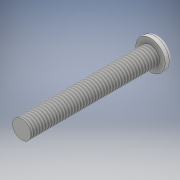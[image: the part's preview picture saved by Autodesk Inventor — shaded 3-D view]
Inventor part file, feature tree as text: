
AUTODESK INVENTOR PART (.ipt)
format: ipt  version: 2018 (Build 220112000, 112)  size: 139,776 bytes
history: native  units: mm
features: sketch x2, revolve x1, fillet x1, extrude x1, thread x1
ambient origin geometry x8: Origin, YZ Plane, XZ Plane, XY Plane, X Axis, Y Axis, Z Axis, Center Point
bodies: Solid1 (feature_tree)
feature tree (6):
  revolve  "Revolution1"  [1 undecoded]
  fillet  "Fillet1"  Radius=2.1mm
  extrude  "Extrusion1"  TaperAngle=90.0deg  [1 undecoded]
  thread  "Thread1"  [1 undecoded]
  sketch  "Sketch1"  dims[d0=2.5mm d1=35.0mm d2=2.1mm]
  sketch  "Sketch2"  dims[d3=4.0mm d4=90.0deg d5=1.0mm d6=0.75mm d7=0.75mm d8=2.7mm d9=2.7mm d10=40.0mm d12=360.0deg d14=1.0mm d15=0.0mm d16=10.0mm d17=0.0mm]
note: 3 required parameter values undecoded (feature->parameter linkage not recoverable at this tier; creation-order binding heuristic only, values carry confidence <= 0.55)